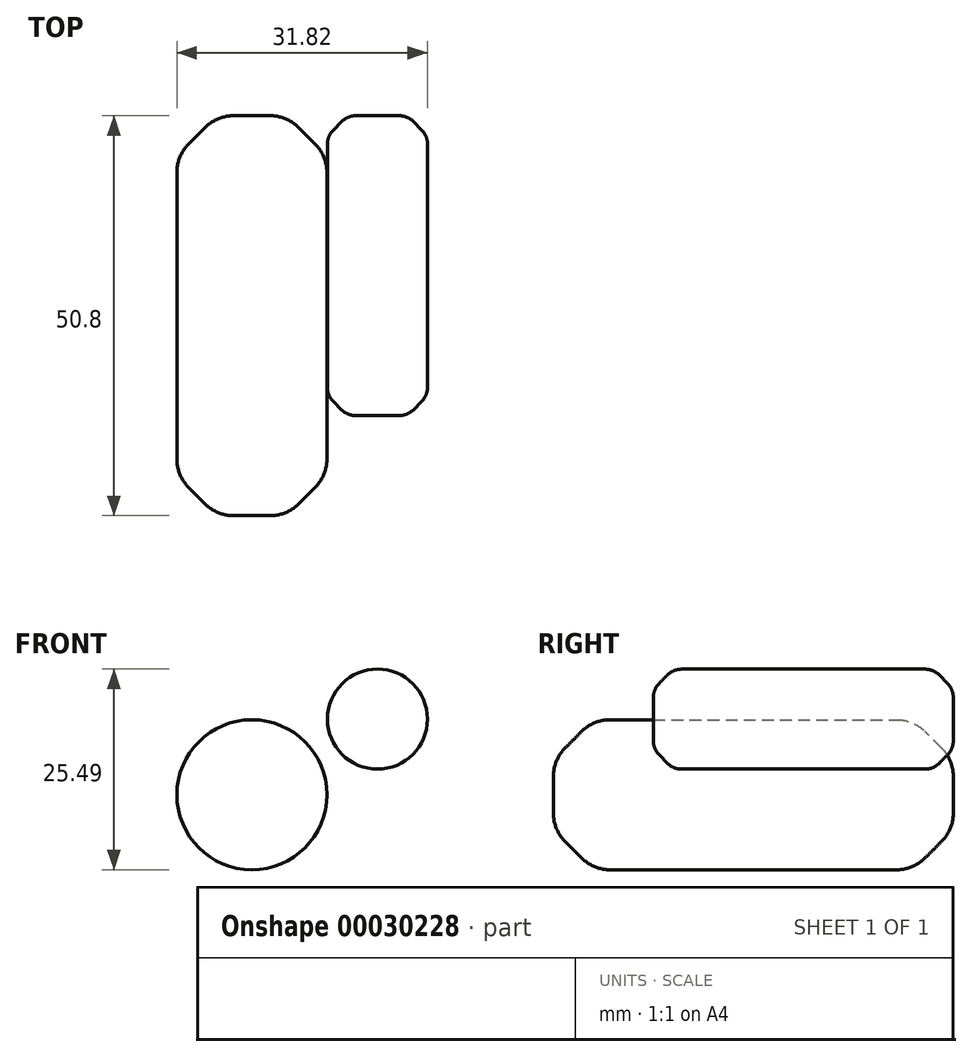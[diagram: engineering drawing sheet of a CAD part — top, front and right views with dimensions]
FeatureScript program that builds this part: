
annotation { "Feature Type Name" : "Feature", "Feature Type Description" : "" }
export const myFeature = defineFeature(function(context is Context, id is Id, definition is map)
    precondition{}
    {
        {
            var Q0;
            Q0=qCreatedBy(makeId("Front.planeOp"),FACE);
            var sketch = newSketch(context, id + "F0", { "sketchPlane" : qUnion([Q0])});
            skCircle(sketch, "E0", {"center": v(-24.08, 42.53) * mm, "radius": 9.53 * mm});
            skCircle(sketch, "E1", {"center": v(-8.14, 52.14) * mm, "radius": 6.35 * mm});
            skSolve(sketch);
        }
        {
            var Q0;
            Q0=makeQuery(id+"F0.imprint","IMPRINT",FACE,{"disambiguationData":[TD([[makeQuery(id+"F0.imprint","IMPRINT",EDGE,{"derivedFrom":sQuery(id+"F0.wireOp",EDGE,"E0")}),1.0]])]});
            extrude(context, id + "F1", {"entities" : qUnion([Q0]), "depth" : 50.8 * mm});
        }
        {
            var Q0;
            Q0=makeQuery(id+"F1.opExtrude","CAP_EDGE",EDGE,{"disambiguationData":[OSD([sQuery(id+"F0.wireOp",EDGE,"E0")])],"isStart":false});
            var Q1;
            Q1=makeQuery(id+"F1.opExtrude","CAP_EDGE",EDGE,{"disambiguationData":[OSD([sQuery(id+"F0.wireOp",EDGE,"E0")])],"isStart":true});
            chamfer(context, id + "F2", {"entities" : qUnion([Q0, Q1]), "width" : 5.08 * mm, "tangentPropagation" : true});
        }
        {
            var Q0;
            {var subQ0=sQuery(id+"F0.wireOp",EDGE,"E0");Q0=makeQuery(id+"F2.opChamfer","BLEND_EDGE",EDGE,{"blendedFrom":[makeQuery(id+"F1.opExtrude","CAP_EDGE",EDGE,{"disambiguationData":[OSD([subQ0])],"isStart":false}),makeQuery(id+"F1.opExtrude","CAP_FACE",FACE,{"disambiguationData":[OSD([subQ0])],"isStart":false})],"blendedInto":[makeQuery(id+"F1.opExtrude","CAP_FACE",FACE,{"disambiguationData":[OSD([subQ0])],"isStart":false})]});}
            var Q1;
            {var subQ0=sQuery(id+"F0.wireOp",EDGE,"E0");Q1=makeQuery(id+"F2.opChamfer","BLEND_EDGE",EDGE,{"blendedFrom":[makeQuery(id+"F1.opExtrude","CAP_EDGE",EDGE,{"disambiguationData":[OSD([subQ0])],"isStart":false}),makeQuery(id+"F1.opExtrude","SWEPT_FACE",FACE,{"disambiguationData":[OSD([subQ0])]})],"blendedInto":[makeQuery(id+"F1.opExtrude","SWEPT_FACE",FACE,{"disambiguationData":[OSD([subQ0])]})]});}
            var Q2;
            {var subQ0=sQuery(id+"F0.wireOp",EDGE,"E0");Q2=makeQuery(id+"F2.opChamfer","BLEND_EDGE",EDGE,{"blendedFrom":[makeQuery(id+"F1.opExtrude","CAP_EDGE",EDGE,{"disambiguationData":[OSD([subQ0])],"isStart":true}),makeQuery(id+"F1.opExtrude","CAP_FACE",FACE,{"disambiguationData":[OSD([subQ0])],"isStart":true})],"blendedInto":[makeQuery(id+"F1.opExtrude","CAP_FACE",FACE,{"disambiguationData":[OSD([subQ0])],"isStart":true})]});}
            var Q3;
            {var subQ0=sQuery(id+"F0.wireOp",EDGE,"E0");Q3=makeQuery(id+"F2.opChamfer","BLEND_EDGE",EDGE,{"blendedFrom":[makeQuery(id+"F1.opExtrude","CAP_EDGE",EDGE,{"disambiguationData":[OSD([subQ0])],"isStart":true}),makeQuery(id+"F1.opExtrude","SWEPT_FACE",FACE,{"disambiguationData":[OSD([subQ0])]})],"blendedInto":[makeQuery(id+"F1.opExtrude","SWEPT_FACE",FACE,{"disambiguationData":[OSD([subQ0])]})]});}
            fillet(context, id + "F3", {"entities" : qUnion([Q0, Q1, Q2, Q3]), "radius" : 5.08 * mm, "tangentPropagation" : true, "allowEdgeOverflow" : false});
        }
        {
            var Q0;
            Q0=makeQuery(id+"F0.imprint","IMPRINT",FACE,{"disambiguationData":[TD([[makeQuery(id+"F0.imprint","IMPRINT",EDGE,{"derivedFrom":sQuery(id+"F0.wireOp",EDGE,"E1")}),1.0]])]});
            extrude(context, id + "F4", {"entities" : qUnion([Q0]), "depth" : 38.1 * mm});
        }
        {
            var Q0;
            Q0=makeQuery(id+"F4.opExtrude","CAP_EDGE",EDGE,{"disambiguationData":[OSD([sQuery(id+"F0.wireOp",EDGE,"E1")])],"isStart":true});
            var Q1;
            Q1=makeQuery(id+"F4.opExtrude","CAP_EDGE",EDGE,{"disambiguationData":[OSD([sQuery(id+"F0.wireOp",EDGE,"E1")])],"isStart":false});
            chamfer(context, id + "F5", {"entities" : qUnion([Q0, Q1]), "width" : 2.54 * mm, "tangentPropagation" : true});
        }
        {
            var Q0;
            {var subQ0=sQuery(id+"F0.wireOp",EDGE,"E1");Q0=makeQuery(id+"F5.opChamfer","BLEND_EDGE",EDGE,{"blendedFrom":[makeQuery(id+"F4.opExtrude","CAP_EDGE",EDGE,{"disambiguationData":[OSD([subQ0])],"isStart":false}),makeQuery(id+"F4.opExtrude","CAP_FACE",FACE,{"disambiguationData":[OSD([subQ0])],"isStart":false})],"blendedInto":[makeQuery(id+"F4.opExtrude","CAP_FACE",FACE,{"disambiguationData":[OSD([subQ0])],"isStart":false})]});}
            var Q1;
            {var subQ0=sQuery(id+"F0.wireOp",EDGE,"E1");Q1=makeQuery(id+"F5.opChamfer","BLEND_FACE",FACE,{"disambiguationData":[OSD([subQ0]),TDD([makeQuery(id+"F4.opExtrude","CAP_EDGE",EDGE,{"disambiguationData":[OSD([subQ0])],"isStart":false})])]});}
            var Q2;
            {var subQ0=sQuery(id+"F0.wireOp",EDGE,"E1");Q2=makeQuery(id+"F5.opChamfer","BLEND_EDGE",EDGE,{"blendedFrom":[makeQuery(id+"F4.opExtrude","CAP_EDGE",EDGE,{"disambiguationData":[OSD([subQ0])],"isStart":true}),makeQuery(id+"F4.opExtrude","SWEPT_FACE",FACE,{"disambiguationData":[OSD([subQ0])]})],"blendedInto":[makeQuery(id+"F4.opExtrude","SWEPT_FACE",FACE,{"disambiguationData":[OSD([subQ0])]})]});}
            var Q3;
            {var subQ0=sQuery(id+"F0.wireOp",EDGE,"E1");Q3=makeQuery(id+"F5.opChamfer","BLEND_EDGE",EDGE,{"blendedFrom":[makeQuery(id+"F4.opExtrude","CAP_EDGE",EDGE,{"disambiguationData":[OSD([subQ0])],"isStart":true}),makeQuery(id+"F4.opExtrude","CAP_FACE",FACE,{"disambiguationData":[OSD([subQ0])],"isStart":true})],"blendedInto":[makeQuery(id+"F4.opExtrude","CAP_FACE",FACE,{"disambiguationData":[OSD([subQ0])],"isStart":true})]});}
            fillet(context, id + "F6", {"entities" : qUnion([Q0, Q1, Q2, Q3]), "radius" : 2.54 * mm, "tangentPropagation" : true, "allowEdgeOverflow" : false});
        }
    });
